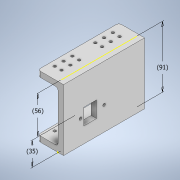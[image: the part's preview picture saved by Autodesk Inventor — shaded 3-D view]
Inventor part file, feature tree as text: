
AUTODESK INVENTOR PART (.ipt)
format: ipt  version: 2020.3 (Build 243373000, 373)  size: 379,392 bytes
history: native  units: mm
features: sketch x5, extrude x5, plane x1, fillet x1
ambient origin geometry x8: Origin, YZ Plane, XZ Plane, XY Plane, X Axis, Y Axis, Z Axis, Center Point
bodies: Body1 (feature_tree)
feature tree (12):
  sketch  "Sketch1"  dims[d15=8.0mm d16=120.0mm]
  extrude  "Extrusion3"  Depth=120.0mm
  extrude  "Extrusion4"  Depth=83.0mm TaperAngle=0.0deg
  extrude  "Extrusion5"  Depth=10.0mm TaperAngle=0.0deg
  plane  "Work Plane1"
  extrude  "Extrusion6"  Depth=4.0mm
  fillet  "Fillet1"  Radius=4.0mm
  extrude  "Extrusion7"  Depth=10.0mm TaperAngle=0.0deg
  sketch  "Sketch6"  dims[d54=4.0mm d55=10.0mm d56=0.0mm d57=91.0mm d58=35.0mm d59=56.0mm d8=0.5mm d9=0.872665mm d10=0.5mm d11=0.872665mm]
  sketch  "Sketch2"  dims[d17=30.0mm d36=83.0mm d37=0.0mm]
  sketch  "Sketch4"  dims[d38=8.0mm d39=0.0mm d45=10.0mm d46=0.0mm]
  sketch  "Sketch5"  dims[d50=8.0mm d51=0.0mm d52=4.0mm d53=4.0mm]
